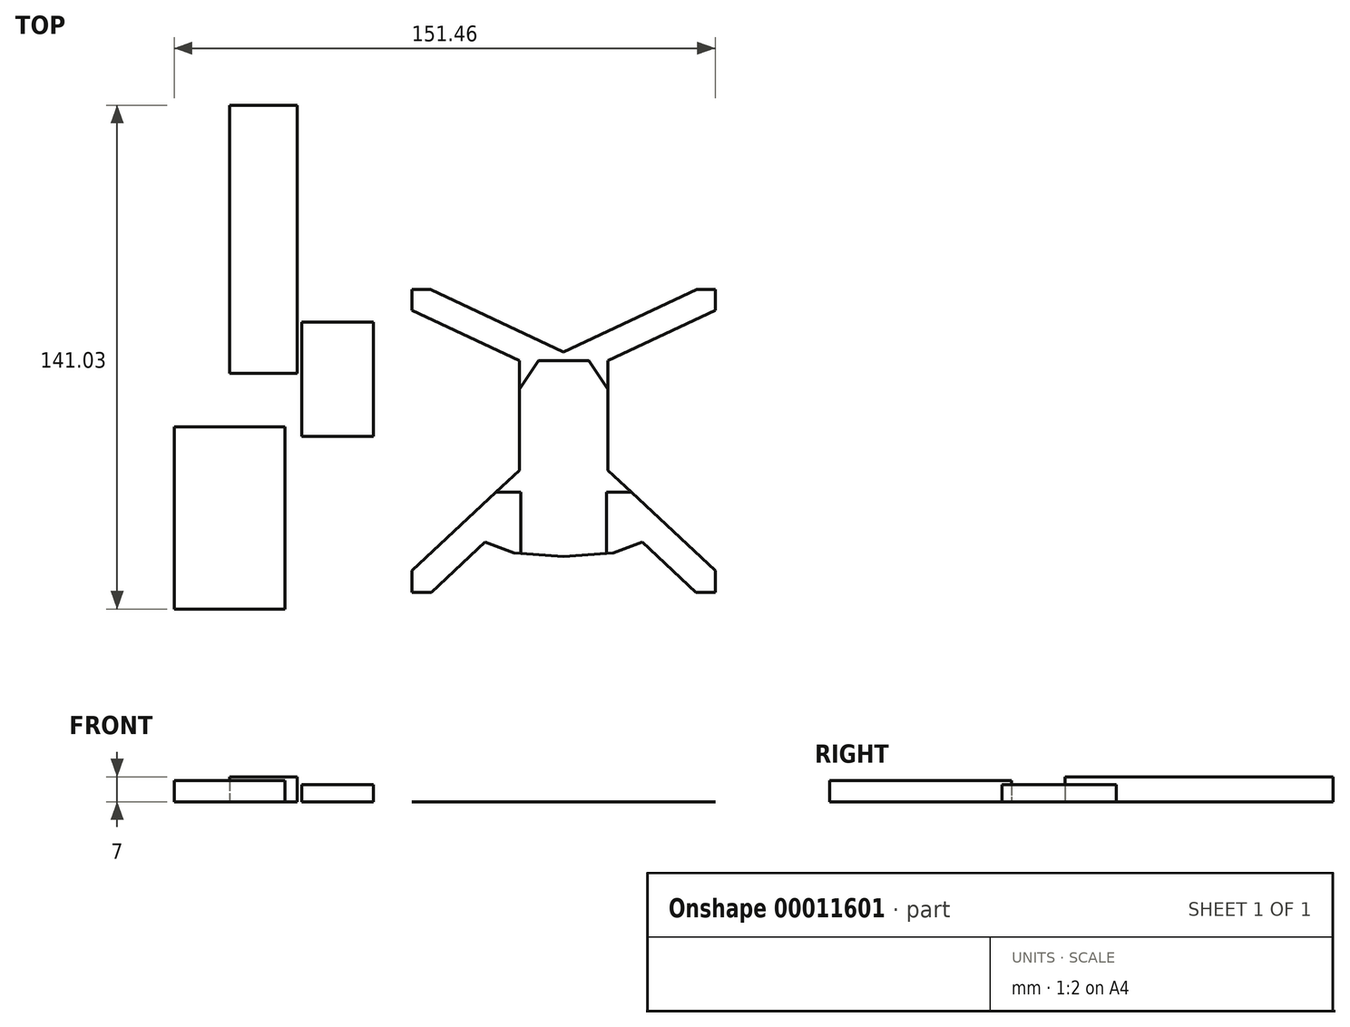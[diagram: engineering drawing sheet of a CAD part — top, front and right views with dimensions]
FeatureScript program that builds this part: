
annotation { "Feature Type Name" : "Feature", "Feature Type Description" : "" }
export const myFeature = defineFeature(function(context is Context, id is Id, definition is map)
    precondition{}
    {
        {
            var Q0;
            Q0=qCreatedBy(makeId("Top.planeOp"),FACE);
            var sketch = newSketch(context, id + "F0", { "sketchPlane" : qUnion([Q0])});
            skLineSegment(sketch, "E0.bottom", {"start": v(-65, 107.43) * mm, "end": v(-46, 107.43) * mm});
            skLineSegment(sketch, "E0.top", {"start": v(-65, 32.43) * mm, "end": v(-46, 32.43) * mm});
            skLineSegment(sketch, "E0.left", {"start": v(-65, 107.43) * mm, "end": v(-65, 32.43) * mm});
            skLineSegment(sketch, "E0.right", {"start": v(-46, 107.43) * mm, "end": v(-46, 32.43) * mm});
            skSolve(sketch);
        }
        {
            var Q0;
            Q0=makeQuery(id+"F0.imprint","IMPRINT",FACE,{"disambiguationData":[TD([[makeQuery(id+"F0.imprint","IMPRINT",EDGE,{"derivedFrom":sQuery(id+"F0.wireOp",EDGE,"E0.bottom")}),-1.0]])]});
            extrude(context, id + "F1", {"entities" : qUnion([Q0]), "depth" : 7 * mm});
        }
        {
            var Q0;
            Q0=qCreatedBy(makeId("Top.planeOp"),FACE);
            var sketch = newSketch(context, id + "F2", { "sketchPlane" : qUnion([Q0])});
            skLineSegment(sketch, "E1.bottom", {"start": v(-49.46, 17.4) * mm, "end": v(-80.46, 17.4) * mm});
            skLineSegment(sketch, "E1.top", {"start": v(-49.46, -33.6) * mm, "end": v(-80.46, -33.6) * mm});
            skLineSegment(sketch, "E1.left", {"start": v(-49.46, 17.4) * mm, "end": v(-49.46, -33.6) * mm});
            skLineSegment(sketch, "E1.right", {"start": v(-80.46, 17.4) * mm, "end": v(-80.46, -33.6) * mm});
            skSolve(sketch);
        }
        {
            var Q0;
            Q0=makeQuery(id+"F2.imprint","IMPRINT",FACE,{"disambiguationData":[TD([[makeQuery(id+"F2.imprint","IMPRINT",EDGE,{"derivedFrom":sQuery(id+"F2.wireOp",EDGE,"E1.bottom")}),1.0]])]});
            extrude(context, id + "F3", {"entities" : qUnion([Q0]), "depth" : 6 * mm});
        }
        {
            var Q0;
            Q0=qCreatedBy(makeId("Top.planeOp"),FACE);
            var sketch = newSketch(context, id + "F4", { "sketchPlane" : qUnion([Q0])});
            skLineSegment(sketch, "E2.bottom", {"start": v(71, 55.94) * mm, "end": v(-13.86, 55.94) * mm});
            skLineSegment(sketch, "E2.top", {"start": v(71, -28.91) * mm, "end": v(-13.86, -28.91) * mm});
            skLineSegment(sketch, "E2.left", {"start": v(71, 55.94) * mm, "end": v(71, -28.91) * mm});
            skLineSegment(sketch, "E2.right", {"start": v(-13.86, 55.94) * mm, "end": v(-13.86, -28.91) * mm});
            skSolve(sketch);
        }
        {
            var Q0;
            Q0 = qSketchRegion(id + "F4", true);
            extrude(context, id + "F5", {"entities" : qUnion([Q0]), "depth" : 3 / 406.4 * mm});
        }
        {
            var Q0;
            Q0=makeQuery(id+"F5.opExtrude","CAP_FACE",FACE,{"disambiguationData":[OSD([sQuery(id+"F4.wireOp",EDGE,"E2.bottom"),sQuery(id+"F4.wireOp",EDGE,"E2.top"),sQuery(id+"F4.wireOp",EDGE,"E2.left"),sQuery(id+"F4.wireOp",EDGE,"E2.right")])],"isStart":false});
            var sketch = newSketch(context, id + "F6", { "sketchPlane" : qUnion([Q0])});
            skLineSegment(sketch, "E3.bottom", {"start": v(-13.86, 35.94) * mm, "end": v(16.14, 35.94) * mm, "construction": true});
            skLineSegment(sketch, "E3.top", {"start": v(-13.86, -0.91) * mm, "end": v(16.14, -0.91) * mm, "construction": true});
            skLineSegment(sketch, "E3.right", {"start": v(16.14, 35.94) * mm, "end": v(16.14, -0.91) * mm, "construction": true});
            skLineSegment(sketch, "E4", {"start": v(28.57, 55.94) * mm, "end": v(28.57, -28.91) * mm, "construction": true});
            skLineSegment(sketch, "E5", {"start": v(-13.86, 35.94) * mm, "end": v(-13.86, -0.91) * mm, "construction": true});
            skLineSegment(sketch, "E6.0.MirrorCS", {"start": v(71, -0.91) * mm, "end": v(41, -0.91) * mm, "construction": true});
            skLineSegment(sketch, "E6.1.MirrorCS", {"start": v(41, 35.94) * mm, "end": v(41, -0.91) * mm, "construction": true});
            skLineSegment(sketch, "E6.2.MirrorCS", {"start": v(71, 35.94) * mm, "end": v(41, 35.94) * mm, "construction": true});
            skLineSegment(sketch, "E6.3.MirrorCS", {"start": v(71, 35.94) * mm, "end": v(71, -0.91) * mm, "construction": true});
            skLineSegment(sketch, "E7", {"start": v(-8.43, -28.91) * mm, "end": v(6.57, -14.91) * mm});
            skLineSegment(sketch, "E8.1.MirrorCS", {"start": v(65.57, -28.91) * mm, "end": v(50.57, -14.91) * mm});
            skLineSegment(sketch, "E9", {"start": v(6.57, -14.91) * mm, "end": v(14.68, -17.91) * mm});
            skLineSegment(sketch, "E10", {"start": v(14.68, -17.91) * mm, "end": v(28.57, -18.91) * mm});
            skLineSegment(sketch, "E11.0.MirrorCS", {"start": v(50.57, -14.91) * mm, "end": v(42.46, -17.91) * mm});
            skLineSegment(sketch, "E11.1.MirrorCS", {"start": v(42.46, -17.91) * mm, "end": v(28.57, -18.91) * mm});
            skLineSegment(sketch, "E12", {"start": v(16.14, 5.2) * mm, "end": v(-13.86, -22.8) * mm});
            skLineSegment(sketch, "E13", {"start": v(-8.43, -28.91) * mm, "end": v(65.57, -28.91) * mm});
            skLineSegment(sketch, "E14.0.MirrorCS", {"start": v(41, 5.2) * mm, "end": v(71, -22.8) * mm});
            skLineSegment(sketch, "E15", {"start": v(16.14, 35.94) * mm, "end": v(-13.86, 50.09) * mm});
            skLineSegment(sketch, "E16", {"start": v(-13.86, 50.09) * mm, "end": v(-13.86, -22.8) * mm});
            skLineSegment(sketch, "E17.0.MirrorCS", {"start": v(41, 35.94) * mm, "end": v(71, 50.09) * mm});
            skLineSegment(sketch, "E18.0.MirrorCS", {"start": v(71, 50.09) * mm, "end": v(71, -22.8) * mm});
            skLineSegment(sketch, "E19", {"start": v(-8.7, 55.94) * mm, "end": v(28.57, 38.36) * mm});
            skLineSegment(sketch, "E20.0.MirrorCS", {"start": v(65.84, 55.94) * mm, "end": v(28.57, 38.36) * mm});
            skLineSegment(sketch, "E21", {"start": v(-8.7, 55.94) * mm, "end": v(65.84, 55.94) * mm});
            skLineSegment(sketch, "E22", {"start": v(16.14, 35.94) * mm, "end": v(16.14, 5.2) * mm});
            skLineSegment(sketch, "E23", {"start": v(41, 35.94) * mm, "end": v(41, 5.2) * mm});
            skSolve(sketch);
        }
        {
            var Q0;
            Q0 = qSketchRegion(id + "F6", true);
            var Q1;
            Q1=makeQuery(id+"F5.opExtrude","CAP_FACE",FACE,{"disambiguationData":[OSD([sQuery(id+"F4.wireOp",EDGE,"E2.bottom"),sQuery(id+"F4.wireOp",EDGE,"E2.top"),sQuery(id+"F4.wireOp",EDGE,"E2.left"),sQuery(id+"F4.wireOp",EDGE,"E2.right")])],"isStart":true});
            extrude(context, id + "F7", {"entities" : qUnion([Q0]), "operationType" : NewBodyOperationType.REMOVE, "endBound" : BoundingType.UP_TO_SURFACE, "oppositeDirection" : true, "endBoundEntityFace" : qUnion([Q1]), "depth" : 25.4 * mm});
        }
        {
            var Q0;
            Q0=makeQuery(id+"F5.opExtrude","CAP_FACE",FACE,{"disambiguationData":[OSD([sQuery(id+"F4.wireOp",EDGE,"E2.bottom"),sQuery(id+"F4.wireOp",EDGE,"E2.top"),sQuery(id+"F4.wireOp",EDGE,"E2.left"),sQuery(id+"F4.wireOp",EDGE,"E2.right")])],"isStart":false});
            var sketch = newSketch(context, id + "F8", { "sketchPlane" : qUnion([Q0])});
            skLineSegment(sketch, "E24", {"start": v(16.14, 35.94) * mm, "end": v(41, 35.94) * mm, "construction": true});
            skLineSegment(sketch, "E25", {"start": v(28.57, 38.36) * mm, "end": v(28.57, -18.91) * mm, "construction": true});
            skLineSegment(sketch, "E26", {"start": v(16.14, 27.94) * mm, "end": v(21.57, 35.94) * mm});
            skLineSegment(sketch, "E27", {"start": v(9.6, -0.91) * mm, "end": v(47.54, -0.91) * mm, "construction": true});
            skLineSegment(sketch, "E28", {"start": v(16.57, -0.91) * mm, "end": v(16.57, -18.05) * mm});
            skLineSegment(sketch, "E29", {"start": v(16.14, 27.94) * mm, "end": v(16.14, 5.2) * mm});
            skLineSegment(sketch, "E30", {"start": v(16.14, 5.2) * mm, "end": v(9.6, -0.91) * mm});
            skLineSegment(sketch, "E31", {"start": v(16.57, -0.91) * mm, "end": v(9.6, -0.91) * mm});
            skLineSegment(sketch, "E32", {"start": v(16.57, -18.05) * mm, "end": v(28.57, -18.91) * mm});
            skLineSegment(sketch, "E33", {"start": v(21.57, 35.94) * mm, "end": v(28.57, 35.94) * mm});
            skLineSegment(sketch, "E34.0.MirrorCS", {"start": v(35.57, 35.94) * mm, "end": v(28.57, 35.94) * mm});
            skLineSegment(sketch, "E35.0.MirrorCS", {"start": v(41, 27.94) * mm, "end": v(35.57, 35.94) * mm});
            skLineSegment(sketch, "E36.0.MirrorCS", {"start": v(41, 27.94) * mm, "end": v(41, 5.2) * mm});
            skLineSegment(sketch, "E37.0.MirrorCS", {"start": v(41, 5.2) * mm, "end": v(47.54, -0.91) * mm});
            skLineSegment(sketch, "E38.0.MirrorCS", {"start": v(40.57, -0.91) * mm, "end": v(47.54, -0.91) * mm});
            skLineSegment(sketch, "E39.0.MirrorCS", {"start": v(40.57, -0.91) * mm, "end": v(40.57, -18.05) * mm});
            skLineSegment(sketch, "E40.0.MirrorCS", {"start": v(40.57, -18.05) * mm, "end": v(28.57, -18.91) * mm});
            skSolve(sketch);
        }
        {
            var Q0;
            Q0 = qSketchRegion(id + "F8", true);
            extrude(context, id + "F9", {"entities" : qUnion([Q0]), "operationType" : NewBodyOperationType.REMOVE, "oppositeDirection" : true, "depth" : 1 / 203.2 * mm});
        }
        {
            var Q0;
            Q0=qCreatedBy(makeId("Top.planeOp"),FACE);
            var sketch = newSketch(context, id + "F10", { "sketchPlane" : qUnion([Q0])});
            skLineSegment(sketch, "E41.bottom", {"start": v(-44.72, 46.68) * mm, "end": v(-24.72, 46.68) * mm});
            skLineSegment(sketch, "E41.top", {"start": v(-44.72, 14.68) * mm, "end": v(-24.72, 14.68) * mm});
            skLineSegment(sketch, "E41.left", {"start": v(-44.72, 46.68) * mm, "end": v(-44.72, 14.68) * mm});
            skLineSegment(sketch, "E41.right", {"start": v(-24.72, 46.68) * mm, "end": v(-24.72, 14.68) * mm});
            skSolve(sketch);
        }
        {
            var Q0;
            Q0=makeQuery(id+"F10.imprint","IMPRINT",FACE,{"disambiguationData":[TD([[makeQuery(id+"F10.imprint","IMPRINT",EDGE,{"derivedFrom":sQuery(id+"F10.wireOp",EDGE,"E41.bottom")}),-1.0]])]});
            extrude(context, id + "F11", {"entities" : qUnion([Q0]), "depth" : 4.8 * mm});
        }
    });
